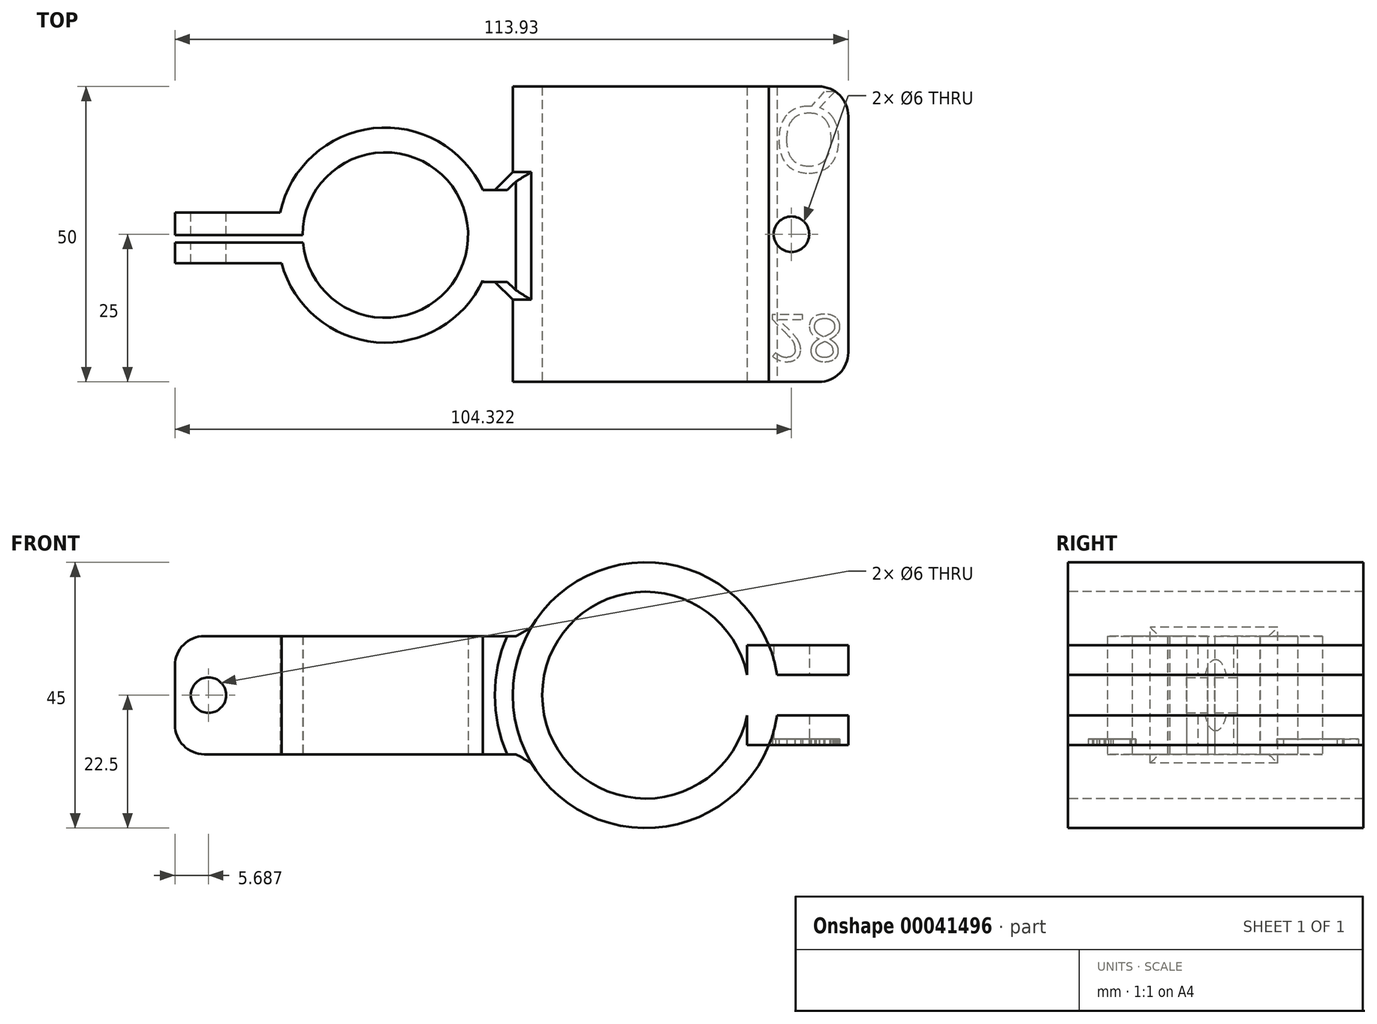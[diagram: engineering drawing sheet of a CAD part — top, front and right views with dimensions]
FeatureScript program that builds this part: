
annotation { "Feature Type Name" : "Feature", "Feature Type Description" : "" }
export const myFeature = defineFeature(function(context is Context, id is Id, definition is map)
    precondition{}
    {
        {
            var Q0;
            Q0=qCreatedBy(makeId("Top.planeOp"),FACE);
            var sketch = newSketch(context, id + "F0", { "sketchPlane" : qUnion([Q0])});
            skArc(sketch, "E0", {"start": v(-13.95, -1.23) * mm, "mid": v(13.99, 0.62) * mm, "end": v(-14, 0) * mm});
            skLineSegment(sketch, "E1.bottom", {"start": v(-14, 0) * mm, "end": v(-35.61, 0) * mm});
            skLineSegment(sketch, "E1.top", {"start": v(-17.8, 3.8) * mm, "end": v(-35.61, 3.8) * mm});
            skLineSegment(sketch, "E1.right", {"start": v(-35.61, 0) * mm, "end": v(-35.61, 3.8) * mm});
            skLineSegment(sketch, "E2.bottom", {"start": v(-13.95, -1.23) * mm, "end": v(-35.61, -1.23) * mm});
            skLineSegment(sketch, "E2.top", {"start": v(-17.57, -4.76) * mm, "end": v(-35.61, -4.76) * mm});
            skLineSegment(sketch, "E2.right", {"start": v(-35.61, -1.23) * mm, "end": v(-35.61, -4.76) * mm});
            skArc(sketch, "E3.trimOffspring", {"start": v(-17.57, -4.76) * mm, "mid": v(-1.54, -18.14) * mm, "end": v(16.51, -7.65) * mm});
            skLineSegment(sketch, "E4.bottom", {"start": v(16.51, 7.65) * mm, "end": v(29.65, 7.65) * mm});
            skLineSegment(sketch, "E4.top", {"start": v(16.51, -7.93) * mm, "end": v(29.65, -7.93) * mm});
            skLineSegment(sketch, "E4.left", {"start": v(16.51, -7.65) * mm, "end": v(16.51, -7.93) * mm});
            skLineSegment(sketch, "E4.right", {"start": v(29.65, 7.65) * mm, "end": v(29.65, -7.93) * mm});
            skArc(sketch, "E5.trimOffspring", {"start": v(16.51, 7.65) * mm, "mid": v(-2.03, 18.09) * mm, "end": v(-17.8, 3.8) * mm});
            skSolve(sketch);
        }
        {
            var Q0;
            Q0=makeQuery(id+"F0.imprint","IMPRINT",FACE,{"disambiguationData":[TD([[makeQuery(id+"F0.imprint","IMPRINT",EDGE,{"derivedFrom":sQuery(id+"F0.wireOp",EDGE,"E0")}),-1.0]])]});
            extrude(context, id + "F1", {"entities" : qUnion([Q0]), "depth" : 20 * mm});
        }
        {
            var Q0;
            Q0=makeQuery(id+"F1.opExtrude","SWEPT_FACE",FACE,{"disambiguationData":[OSD([sQuery(id+"F0.wireOp",EDGE,"E1.top")])]});
            var sketch = newSketch(context, id + "F2", { "sketchPlane" : qUnion([Q0])});
            skCircle(sketch, "E6", {"center": v(29.92, 10) * mm, "radius": 3 * mm});
            skPoint(sketch, "E6.centerSnap0", {"position": v(35.61, 10) * mm});
            skSolve(sketch);
        }
        {
            var Q0;
            Q0=makeQuery(id+"F2.imprint","IMPRINT",FACE,{"disambiguationData":[TD([[makeQuery(id+"F2.imprint","IMPRINT",EDGE,{"derivedFrom":sQuery(id+"F2.wireOp",EDGE,"E6")}),1.0]])]});
            extrude(context, id + "F3", {"entities" : qUnion([Q0]), "operationType" : NewBodyOperationType.REMOVE, "endBound" : BoundingType.THROUGH_ALL, "oppositeDirection" : true, "depth" : 25 * mm});
        }
        {
            var Q0;
            Q0=makeQuery(id+"F1.opExtrude","SWEPT_FACE",FACE,{"disambiguationData":[OSD([sQuery(id+"F0.wireOp",EDGE,"E4.bottom")])]});
            var sketch = newSketch(context, id + "F4", { "sketchPlane" : qUnion([Q0])});
            skCircle(sketch, "E7", {"center": v(-44.04, 10) * mm, "radius": 22.5 * mm});
            skPoint(sketch, "E7.centerSnap0", {"position": v(-29.65, 10) * mm});
            skCircle(sketch, "E8", {"center": v(-44.04, 10) * mm, "radius": 17.5 * mm});
            skSolve(sketch);
        }
        {
            var Q0;
            {var subQ0=sQuery(id+"F0.wireOp",EDGE,"E4.bottom");var subQ1=makeQuery(id+"F1.opExtrude","CAP_EDGE",EDGE,{"disambiguationData":[OSD([subQ0])],"isStart":true});var subQ9=sQuery(id+"F4.wireOp",EDGE,"E7");var subQ10=makeQuery(id+"F4.imprint","INTERSECT",VERTEX,{"derivedFrom":[subQ1,subQ9]});Q0=makeQuery(id+"F4.imprint","IMPRINT",FACE,{"disambiguationData":[TD([[makeQuery(id+"F4.imprint","IMPRINT",EDGE,{"disambiguationData":[TD([[subQ10,1.0]])],"derivedFrom":subQ9}),1.0]])]});}
            var Q1;
            {var subQ0=sQuery(id+"F0.wireOp",EDGE,"E4.bottom");var subQ7=makeQuery(id+"F1.opExtrude","CAP_EDGE",EDGE,{"disambiguationData":[OSD([subQ0])],"isStart":true});var subQ9=sQuery(id+"F4.wireOp",EDGE,"E7");var subQ10=makeQuery(id+"F4.imprint","INTERSECT",VERTEX,{"derivedFrom":[subQ7,subQ9]});Q1=makeQuery(id+"F4.imprint","IMPRINT",FACE,{"disambiguationData":[TD([[makeQuery(id+"F4.imprint","IMPRINT",EDGE,{"disambiguationData":[TD([[subQ10,-1.0]])],"derivedFrom":subQ9}),1.0]])]});}
            var Q2;
            Q2=sQuery(id+"F4.wireOp",EDGE,"E7");
            extrude(context, id + "F5", {"entities" : qUnion([Q0, Q1]), "operationType" : NewBodyOperationType.ADD, "surfaceEntities" : qUnion([Q2]), "depth" : 35 * mm, "symmetric" : true});
        }
        {
            var Q0;
            Q0=makeQuery(id+"F5.boolean.opBoolean","SPLIT",FACE,{"disambiguationData":[TD([makeQuery(id+"F1.opExtrude","SWEPT_FACE",FACE,{"disambiguationData":[OSD([sQuery(id+"F0.wireOp",EDGE,"E4.right")])]})])],"derivedFrom":makeQuery(id+"F1.opExtrude","SWEPT_FACE",FACE,{"disambiguationData":[OSD([sQuery(id+"F0.wireOp",EDGE,"E4.top")])]})});
            extrude(context, id + "F6", {"entities" : qUnion([Q0]), "operationType" : NewBodyOperationType.REMOVE, "oppositeDirection" : true, "depth" : 25 * mm});
        }
        {
            var Q0;
            Q0=makeQuery(id+"F5.opExtrude","CAP_FACE",FACE,{"disambiguationData":[OSD([sQuery(id+"F4.wireOp",EDGE,"E7"),sQuery(id+"F4.wireOp",EDGE,"E8")])],"isStart":true});
            var sketch = newSketch(context, id + "F7", { "sketchPlane" : qUnion([Q0])});
            skLineSegment(sketch, "E9.bottom", {"start": v(61.2, 6.57) * mm, "end": v(78.32, 6.57) * mm});
            skLineSegment(sketch, "E9.top", {"start": v(61.2, 1.57) * mm, "end": v(78.32, 1.57) * mm});
            skLineSegment(sketch, "E9.left", {"start": v(61.2, 6.57) * mm, "end": v(61.2, 1.57) * mm});
            skLineSegment(sketch, "E9.right", {"start": v(78.32, 6.57) * mm, "end": v(78.32, 1.57) * mm});
            skPoint(sketch, "E10.oppositeSnap0", {"position": v(78.32, 4.07) * mm});
            skLineSegment(sketch, "E10.bottom", {"start": v(61.2, 13.43) * mm, "end": v(78.32, 13.43) * mm});
            skLineSegment(sketch, "E10.top", {"start": v(61.2, 18.43) * mm, "end": v(78.32, 18.43) * mm});
            skLineSegment(sketch, "E10.left", {"start": v(61.2, 13.43) * mm, "end": v(61.2, 18.43) * mm});
            skLineSegment(sketch, "E10.right", {"start": v(78.32, 13.43) * mm, "end": v(78.32, 18.43) * mm});
            skLineSegment(sketch, "E11.bottom", {"start": v(68.43, 6.57) * mm, "end": v(58.22, 6.57) * mm});
            skLineSegment(sketch, "E11.top", {"start": v(68.43, 13.43) * mm, "end": v(58.22, 13.43) * mm});
            skLineSegment(sketch, "E11.left", {"start": v(68.43, 6.57) * mm, "end": v(68.43, 13.43) * mm});
            skLineSegment(sketch, "E11.right", {"start": v(58.22, 6.57) * mm, "end": v(58.22, 13.43) * mm});
            skSolve(sketch);
        }
        {
            var Q0;
            {var subQ0=sQuery(id+"F7.wireOp",EDGE,"E11.bottom");var subQ3=makeQuery(id+"F5.opExtrude","CAP_EDGE",EDGE,{"disambiguationData":[OSD([sQuery(id+"F4.wireOp",EDGE,"E7")])],"isStart":true});var subQ4=makeQuery(id+"F7.imprint","INTERSECT",VERTEX,{"derivedFrom":[subQ3,subQ0]});Q0=makeQuery(id+"F7.imprint","IMPRINT",FACE,{"disambiguationData":[TD([[makeQuery(id+"F7.imprint","IMPRINT",EDGE,{"disambiguationData":[TD([[subQ4,1.0]])],"derivedFrom":subQ3}),-1.0]])]});}
            var Q1;
            Q1=makeQuery(id+"F5.opExtrude","CAP_FACE",FACE,{"disambiguationData":[OSD([sQuery(id+"F4.wireOp",EDGE,"E7"),sQuery(id+"F4.wireOp",EDGE,"E8")])],"isStart":false});
            extrude(context, id + "F8", {"entities" : qUnion([Q0]), "operationType" : NewBodyOperationType.REMOVE, "endBound" : BoundingType.UP_TO_SURFACE, "oppositeDirection" : true, "endBoundEntityFace" : qUnion([Q1]), "depth" : 25 * mm});
        }
        {
            var Q0;
            {var subQ0=sQuery(id+"F7.wireOp",EDGE,"E9.right");Q0=makeQuery(id+"F7.imprint","IMPRINT",FACE,{"disambiguationData":[TD([[makeQuery(id+"F7.imprint","IMPRINT",EDGE,{"derivedFrom":subQ0}),-1.0]])]});}
            var Q1;
            {var subQ0=sQuery(id+"F7.wireOp",EDGE,"E10.right");Q1=makeQuery(id+"F7.imprint","IMPRINT",FACE,{"disambiguationData":[TD([[makeQuery(id+"F7.imprint","IMPRINT",EDGE,{"derivedFrom":subQ0}),1.0]])]});}
            var Q2;
            Q2=makeQuery(id+"F5.opExtrude","CAP_FACE",FACE,{"disambiguationData":[OSD([sQuery(id+"F4.wireOp",EDGE,"E7"),sQuery(id+"F4.wireOp",EDGE,"E8")])],"isStart":false});
            extrude(context, id + "F9", {"entities" : qUnion([Q0, Q1]), "operationType" : NewBodyOperationType.ADD, "endBound" : BoundingType.UP_TO_SURFACE, "oppositeDirection" : true, "endBoundEntityFace" : qUnion([Q2]), "depth" : 25 * mm});
        }
        {
            var Q0;
            {var subQ0=sQuery(id+"F4.wireOp",EDGE,"E7");Q0=makeQuery(id+"F9.boolean.opBoolean","MERGE",FACE,{"derivedFrom":[makeQuery(id+"F5.opExtrude","CAP_FACE",FACE,{"disambiguationData":[OSD([subQ0,sQuery(id+"F4.wireOp",EDGE,"E8")])],"isStart":true}),makeQuery(id+"F9.opExtrude","CAP_FACE",FACE,{"disambiguationData":[OSD([subQ0,sQuery(id+"F7.wireOp",EDGE,"E9.bottom"),sQuery(id+"F7.wireOp",EDGE,"E9.top"),sQuery(id+"F7.wireOp",EDGE,"E9.right"),sQuery(id+"F7.wireOp",EDGE,"E11.bottom")])],"isStart":true}),makeQuery(id+"F9.opExtrude","CAP_FACE",FACE,{"disambiguationData":[OSD([subQ0,sQuery(id+"F7.wireOp",EDGE,"E10.bottom"),sQuery(id+"F7.wireOp",EDGE,"E10.top"),sQuery(id+"F7.wireOp",EDGE,"E10.right"),sQuery(id+"F7.wireOp",EDGE,"E11.top")])],"isStart":true})]});}
            extrude(context, id + "F10", {"entities" : qUnion([Q0]), "operationType" : NewBodyOperationType.ADD, "depth" : 15 * mm});
        }
        {
            var Q0;
            Q0=makeQuery(id+"F5.boolean.opBoolean","INTERSECT",EDGE,{"derivedFrom":[makeQuery(id+"F1.opExtrude","CAP_FACE",FACE,{"disambiguationData":[OSD([sQuery(id+"F0.wireOp",EDGE,"E0"),sQuery(id+"F0.wireOp",EDGE,"E1.bottom"),sQuery(id+"F0.wireOp",EDGE,"E1.top"),sQuery(id+"F0.wireOp",EDGE,"E1.right"),sQuery(id+"F0.wireOp",EDGE,"E2.bottom"),sQuery(id+"F0.wireOp",EDGE,"E2.top"),sQuery(id+"F0.wireOp",EDGE,"E2.right"),sQuery(id+"F0.wireOp",EDGE,"E3.trimOffspring"),sQuery(id+"F0.wireOp",EDGE,"E4.bottom"),sQuery(id+"F0.wireOp",EDGE,"E4.top"),sQuery(id+"F0.wireOp",EDGE,"E4.left"),sQuery(id+"F0.wireOp",EDGE,"E4.right"),sQuery(id+"F0.wireOp",EDGE,"E5.trimOffspring")])],"isStart":true}),makeQuery(id+"F5.opExtrude","SWEPT_FACE",FACE,{"disambiguationData":[OSD([sQuery(id+"F4.wireOp",EDGE,"E7")])]})]});
            var Q1;
            Q1=makeQuery(id+"F5.boolean.opBoolean","INTERSECT",EDGE,{"derivedFrom":[makeQuery(id+"F1.opExtrude","CAP_FACE",FACE,{"disambiguationData":[OSD([sQuery(id+"F0.wireOp",EDGE,"E0"),sQuery(id+"F0.wireOp",EDGE,"E1.bottom"),sQuery(id+"F0.wireOp",EDGE,"E1.top"),sQuery(id+"F0.wireOp",EDGE,"E1.right"),sQuery(id+"F0.wireOp",EDGE,"E2.bottom"),sQuery(id+"F0.wireOp",EDGE,"E2.top"),sQuery(id+"F0.wireOp",EDGE,"E2.right"),sQuery(id+"F0.wireOp",EDGE,"E3.trimOffspring"),sQuery(id+"F0.wireOp",EDGE,"E4.bottom"),sQuery(id+"F0.wireOp",EDGE,"E4.top"),sQuery(id+"F0.wireOp",EDGE,"E4.left"),sQuery(id+"F0.wireOp",EDGE,"E4.right"),sQuery(id+"F0.wireOp",EDGE,"E5.trimOffspring")])],"isStart":false}),makeQuery(id+"F5.opExtrude","SWEPT_FACE",FACE,{"disambiguationData":[OSD([sQuery(id+"F4.wireOp",EDGE,"E7")])]})]});
            var Q2;
            Q2=makeQuery(id+"F5.boolean.opBoolean","INTERSECT",EDGE,{"derivedFrom":[makeQuery(id+"F1.opExtrude","SWEPT_FACE",FACE,{"disambiguationData":[OSD([sQuery(id+"F0.wireOp",EDGE,"E4.bottom")])]}),makeQuery(id+"F5.opExtrude","SWEPT_FACE",FACE,{"disambiguationData":[OSD([sQuery(id+"F4.wireOp",EDGE,"E7")])]})]});
            var Q3;
            Q3=makeQuery(id+"F5.boolean.opBoolean","INTERSECT",EDGE,{"derivedFrom":[makeQuery(id+"F1.opExtrude","SWEPT_FACE",FACE,{"disambiguationData":[OSD([sQuery(id+"F0.wireOp",EDGE,"E4.top")])]}),makeQuery(id+"F5.opExtrude","SWEPT_FACE",FACE,{"disambiguationData":[OSD([sQuery(id+"F4.wireOp",EDGE,"E7")])]})]});
            chamfer(context, id + "F11", {"entities" : qUnion([Q0, Q1, Q2, Q3]), "width" : 3 * mm});
        }
        {
            var Q0;
            {var subQ0=sQuery(id+"F7.wireOp",EDGE,"E9.top");Q0=makeQuery(id+"F10.boolean.opBoolean","MERGE",FACE,{"derivedFrom":[makeQuery(id+"F9.opExtrude","SWEPT_FACE",FACE,{"disambiguationData":[OSD([subQ0])]}),makeQuery(id+"F10.opExtrude","SWEPT_FACE",FACE,{"disambiguationData":[OSD([subQ0])]})]});}
            var sketch = newSketch(context, id + "F12", { "sketchPlane" : qUnion([Q0])});
            skCircle(sketch, "E12", {"center": v(68.71, -0.15) * mm, "radius": 3 * mm});
            skPoint(sketch, "E12.centerSnap0", {"position": v(78.32, -0.15) * mm});
            skSolve(sketch);
        }
        {
            var Q0;
            Q0 = qSketchRegion(id + "F12", true);
            extrude(context, id + "F13", {"entities" : qUnion([Q0]), "operationType" : NewBodyOperationType.REMOVE, "oppositeDirection" : true, "depth" : 25 * mm});
        }
        {
            var Q0;
            Q0=makeQuery(id+"F1.opExtrude","CAP_EDGE",EDGE,{"disambiguationData":[OSD([sQuery(id+"F0.wireOp",EDGE,"E2.right")])],"isStart":true});
            var Q1;
            Q1=makeQuery(id+"F1.opExtrude","CAP_EDGE",EDGE,{"disambiguationData":[OSD([sQuery(id+"F0.wireOp",EDGE,"E1.right")])],"isStart":true});
            var Q2;
            Q2=makeQuery(id+"F1.opExtrude","CAP_EDGE",EDGE,{"disambiguationData":[OSD([sQuery(id+"F0.wireOp",EDGE,"E2.right")])],"isStart":false});
            var Q3;
            Q3=makeQuery(id+"F1.opExtrude","CAP_EDGE",EDGE,{"disambiguationData":[OSD([sQuery(id+"F0.wireOp",EDGE,"E1.right")])],"isStart":false});
            var Q4;
            Q4=makeQuery(id+"F9.opExtrude","CAP_EDGE",EDGE,{"disambiguationData":[OSD([sQuery(id+"F7.wireOp",EDGE,"E9.right")])],"isStart":true});
            var Q5;
            Q5=makeQuery(id+"F9.opExtrude","CAP_EDGE",EDGE,{"disambiguationData":[OSD([sQuery(id+"F7.wireOp",EDGE,"E10.right")])],"isStart":true});
            var Q6;
            Q6=makeQuery(id+"F9.opExtrude","CAP_EDGE",EDGE,{"disambiguationData":[OSD([sQuery(id+"F7.wireOp",EDGE,"E10.right")])],"isStart":false});
            var Q7;
            Q7=makeQuery(id+"F9.opExtrude","CAP_EDGE",EDGE,{"disambiguationData":[OSD([sQuery(id+"F7.wireOp",EDGE,"E9.right")])],"isStart":false});
            var Q8;
            Q8=makeQuery(id+"F10.opExtrude","CAP_EDGE",EDGE,{"disambiguationData":[OSD([sQuery(id+"F7.wireOp",EDGE,"E9.right")])],"isStart":false});
            var Q9;
            Q9=makeQuery(id+"F10.opExtrude","CAP_EDGE",EDGE,{"disambiguationData":[OSD([sQuery(id+"F7.wireOp",EDGE,"E10.right")])],"isStart":false});
            fillet(context, id + "F14", {"entities" : qUnion([Q0, Q1, Q2, Q3, Q4, Q5, Q6, Q7, Q8, Q9]), "radius" : 5 * mm, "tangentPropagation" : true, "allowEdgeOverflow" : false});
        }
        {
            var Q0;
            {var subQ0=sQuery(id+"F7.wireOp",EDGE,"E9.top");Q0=makeQuery(id+"F10.boolean.opBoolean","MERGE",FACE,{"derivedFrom":[makeQuery(id+"F9.opExtrude","SWEPT_FACE",FACE,{"disambiguationData":[OSD([subQ0])]}),makeQuery(id+"F10.opExtrude","SWEPT_FACE",FACE,{"disambiguationData":[OSD([subQ0])]})]});}
            var sketch = newSketch(context, id + "F15", { "sketchPlane" : qUnion([Q0])});
            skText(sketch, "E13", { "text": "28", "fontName": "OpenSans-Regular.ttf"});
            skText(sketch, "E14", { "text": "Q", "fontName": "OpenSans-Regular.ttf"});
            const initialGuessF15  = {"E13": [0.0649, 0.01348, 1, 0, 0.00791], "E14": [0.06564, -0.02166, 1, 0, 0.0111]};
            skSetInitialGuess(sketch, initialGuessF15);
            skSolve(sketch);
        }
        {
            var Q0;
            Q0 = qSketchRegion(id + "F15", true);
            extrude(context, id + "F16", {"entities" : qUnion([Q0]), "operationType" : NewBodyOperationType.REMOVE, "oppositeDirection" : true, "depth" : 1 * mm});
        }
    });
